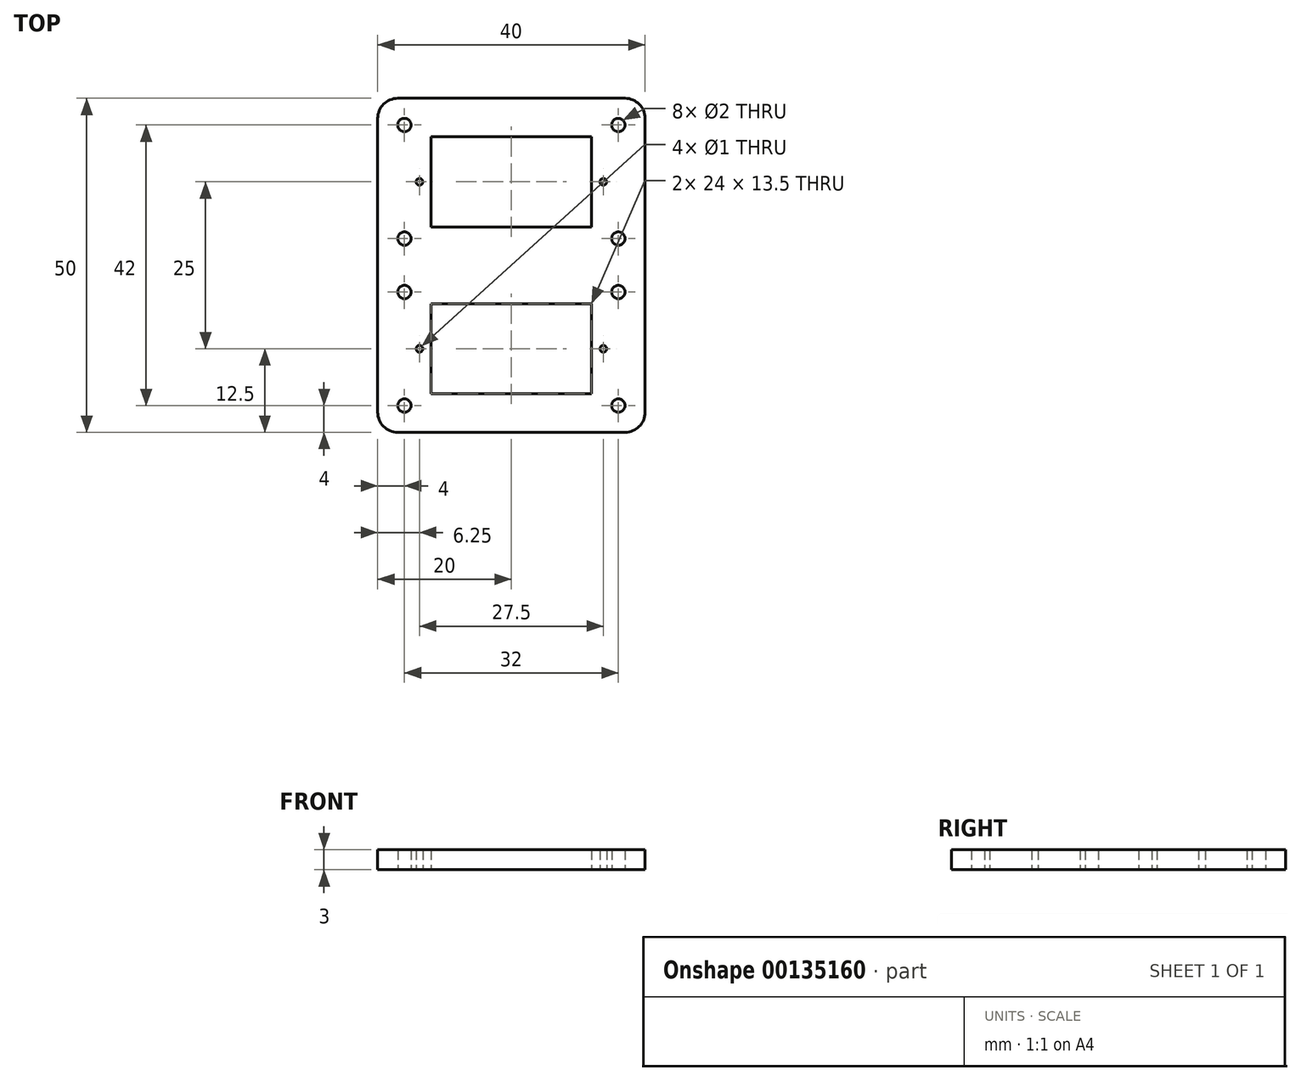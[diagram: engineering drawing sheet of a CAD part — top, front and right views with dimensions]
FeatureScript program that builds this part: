
annotation { "Feature Type Name" : "Feature", "Feature Type Description" : "" }
export const myFeature = defineFeature(function(context is Context, id is Id, definition is map)
    precondition{}
    {
        {
            var Q0;
            Q0=qCreatedBy(makeId("Top.planeOp"),FACE);
            var sketch = newSketch(context, id + "F0", { "sketchPlane" : qUnion([Q0])});
            skLineSegment(sketch, "E0.bottom", {"start": v(12, -6.75) * mm, "end": v(-12, -6.75) * mm});
            skLineSegment(sketch, "E0.top", {"start": v(12, 6.75) * mm, "end": v(-12, 6.75) * mm});
            skLineSegment(sketch, "E0.left", {"start": v(12, -6.75) * mm, "end": v(12, 6.75) * mm});
            skLineSegment(sketch, "E0.right", {"start": v(-12, -6.75) * mm, "end": v(-12, 6.75) * mm});
            skPoint(sketch, "E0.middle", {"position": v(0, 0) * mm});
            skLineSegment(sketch, "E1.bottom", {"start": v(13.75, 0) * mm, "end": v(-13.75, 0) * mm, "construction": true});
            skLineSegment(sketch, "E1.top", {"start": v(13.75, 0) * mm, "end": v(-13.75, 0) * mm, "construction": true});
            skLineSegment(sketch, "E1.left", {"start": v(13.75, 0) * mm, "end": v(13.75, 0) * mm});
            skLineSegment(sketch, "E1.right", {"start": v(-13.75, 0) * mm, "end": v(-13.75, 0) * mm});
            skLineSegment(sketch, "E2.bottom", {"start": v(20, 12.5) * mm, "end": v(-20, 12.5) * mm});
            skLineSegment(sketch, "E2.top", {"start": v(20, -12.5) * mm, "end": v(-20, -12.5) * mm});
            skLineSegment(sketch, "E2.left", {"start": v(20, 12.5) * mm, "end": v(20, -12.5) * mm});
            skLineSegment(sketch, "E2.right", {"start": v(-20, 12.5) * mm, "end": v(-20, -12.5) * mm});
            skPoint(sketch, "E3.middle", {"position": v(-20, 12.5) * mm});
            skLineSegment(sketch, "E4.bottom", {"start": v(-20, 12.5) * mm, "end": v(-16, 12.5) * mm, "construction": true});
            skLineSegment(sketch, "E4.top", {"start": v(-20, 8.5) * mm, "end": v(-16, 8.5) * mm, "construction": true});
            skLineSegment(sketch, "E4.left", {"start": v(-20, 12.5) * mm, "end": v(-20, 8.5) * mm, "construction": true});
            skLineSegment(sketch, "E4.right", {"start": v(-16, 12.5) * mm, "end": v(-16, 8.5) * mm, "construction": true});
            skLineSegment(sketch, "E5.bottom", {"start": v(20, 12.5) * mm, "end": v(16, 12.5) * mm});
            skLineSegment(sketch, "E5.top", {"start": v(20, 8.5) * mm, "end": v(16, 8.5) * mm, "construction": true});
            skLineSegment(sketch, "E5.left", {"start": v(20, 12.5) * mm, "end": v(20, 8.5) * mm, "construction": true});
            skLineSegment(sketch, "E5.right", {"start": v(16, 12.5) * mm, "end": v(16, 8.5) * mm, "construction": true});
            skLineSegment(sketch, "E6.bottom", {"start": v(20, -12.5) * mm, "end": v(16, -12.5) * mm});
            skLineSegment(sketch, "E6.top", {"start": v(20, -8.5) * mm, "end": v(16, -8.5) * mm, "construction": true});
            skLineSegment(sketch, "E6.left", {"start": v(20, -12.5) * mm, "end": v(20, -8.5) * mm});
            skLineSegment(sketch, "E6.right", {"start": v(16, -12.5) * mm, "end": v(16, -8.5) * mm, "construction": true});
            skLineSegment(sketch, "E7.bottom", {"start": v(-20, -12.5) * mm, "end": v(-16, -12.5) * mm});
            skLineSegment(sketch, "E7.top", {"start": v(-20, -8.5) * mm, "end": v(-16, -8.5) * mm, "construction": true});
            skLineSegment(sketch, "E7.left", {"start": v(-20, -12.5) * mm, "end": v(-20, -8.5) * mm});
            skLineSegment(sketch, "E7.right", {"start": v(-16, -12.5) * mm, "end": v(-16, -8.5) * mm, "construction": true});
            skCircle(sketch, "E8", {"center": v(-16, 8.5) * mm, "radius": 1 * mm});
            skCircle(sketch, "E9", {"center": v(16, 8.5) * mm, "radius": 1 * mm});
            skCircle(sketch, "E10", {"center": v(16, -8.5) * mm, "radius": 1 * mm});
            skCircle(sketch, "E11", {"center": v(-16, -8.5) * mm, "radius": 1 * mm});
            skCircle(sketch, "E12", {"center": v(-13.75, 0) * mm, "radius": 0.5 * mm});
            skCircle(sketch, "E13", {"center": v(13.75, 0) * mm, "radius": 0.5 * mm});
            skSolve(sketch);
        }
        {
            var Q0;
            Q0=makeQuery(id+"F0.imprint","IMPRINT",FACE,{"disambiguationData":[TD([[makeQuery(id+"F0.imprint","IMPRINT",EDGE,{"derivedFrom":sQuery(id+"F0.wireOp",EDGE,"E0.bottom")}),1.0]])]});
            extrude(context, id + "F1", {"entities" : qUnion([Q0]), "depth" : 3 * mm});
        }
        {
            var Q0;
            Q0=makeQuery(id+"F1.opExtrude","SWEPT_BODY",BODY,{"disambiguationData":[OSD([sQuery(id+"F0.wireOp",EDGE,"E0.bottom"),sQuery(id+"F0.wireOp",EDGE,"E0.top"),sQuery(id+"F0.wireOp",EDGE,"E0.left"),sQuery(id+"F0.wireOp",EDGE,"E0.right"),sQuery(id+"F0.wireOp",EDGE,"E2.bottom"),sQuery(id+"F0.wireOp",EDGE,"E2.top"),sQuery(id+"F0.wireOp",EDGE,"E2.left"),sQuery(id+"F0.wireOp",EDGE,"E2.right"),sQuery(id+"F0.wireOp",EDGE,"E5.bottom"),sQuery(id+"F0.wireOp",EDGE,"E6.bottom"),sQuery(id+"F0.wireOp",EDGE,"E6.left"),sQuery(id+"F0.wireOp",EDGE,"E7.bottom"),sQuery(id+"F0.wireOp",EDGE,"E7.left"),sQuery(id+"F0.wireOp",EDGE,"E8"),sQuery(id+"F0.wireOp",EDGE,"E9"),sQuery(id+"F0.wireOp",EDGE,"E10"),sQuery(id+"F0.wireOp",EDGE,"E11"),sQuery(id+"F0.wireOp",EDGE,"E12"),sQuery(id+"F0.wireOp",EDGE,"E13")])]});
            var Q1;
            Q1=makeQuery(id+"F1.opExtrude","SWEPT_FACE",FACE,{"disambiguationData":[OSD([sQuery(id+"F0.wireOp",EDGE,"E2.top"),sQuery(id+"F0.wireOp",EDGE,"E6.bottom"),sQuery(id+"F0.wireOp",EDGE,"E7.bottom")])]});
            mirror(context, id + "F2", {"operationType" : NewBodyOperationType.ADD, "entities" : qUnion([Q0]), "mirrorPlane" : qUnion([Q1])});
        }
        {
            var Q0;
            Q0=makeQuery(id+"F2.opPattern","COPY",EDGE,{"derivedFrom":makeQuery(id+"F1.opExtrude","SWEPT_EDGE",EDGE,{"disambiguationData":[OSD([sQuery(id+"F0.wireOp",EDGE,"E2.bottom"),sQuery(id+"F0.wireOp",EDGE,"E2.right")])]}),"instanceName":"1"});
            var Q1;
            Q1=makeQuery(id+"F2.opPattern","COPY",EDGE,{"derivedFrom":makeQuery(id+"F1.opExtrude","SWEPT_EDGE",EDGE,{"disambiguationData":[OSD([sQuery(id+"F0.wireOp",EDGE,"E2.left"),sQuery(id+"F0.wireOp",EDGE,"E5.bottom")])]}),"instanceName":"1"});
            var Q2;
            Q2=makeQuery(id+"F1.opExtrude","SWEPT_EDGE",EDGE,{"disambiguationData":[OSD([sQuery(id+"F0.wireOp",EDGE,"E2.left"),sQuery(id+"F0.wireOp",EDGE,"E5.bottom")])]});
            var Q3;
            Q3=makeQuery(id+"F1.opExtrude","SWEPT_EDGE",EDGE,{"disambiguationData":[OSD([sQuery(id+"F0.wireOp",EDGE,"E2.bottom"),sQuery(id+"F0.wireOp",EDGE,"E2.right")])]});
            fillet(context, id + "F3", {"entities" : qUnion([Q0, Q1, Q2, Q3]), "radius" : 3 * mm, "tangentPropagation" : true, "allowEdgeOverflow" : false});
        }
    });
